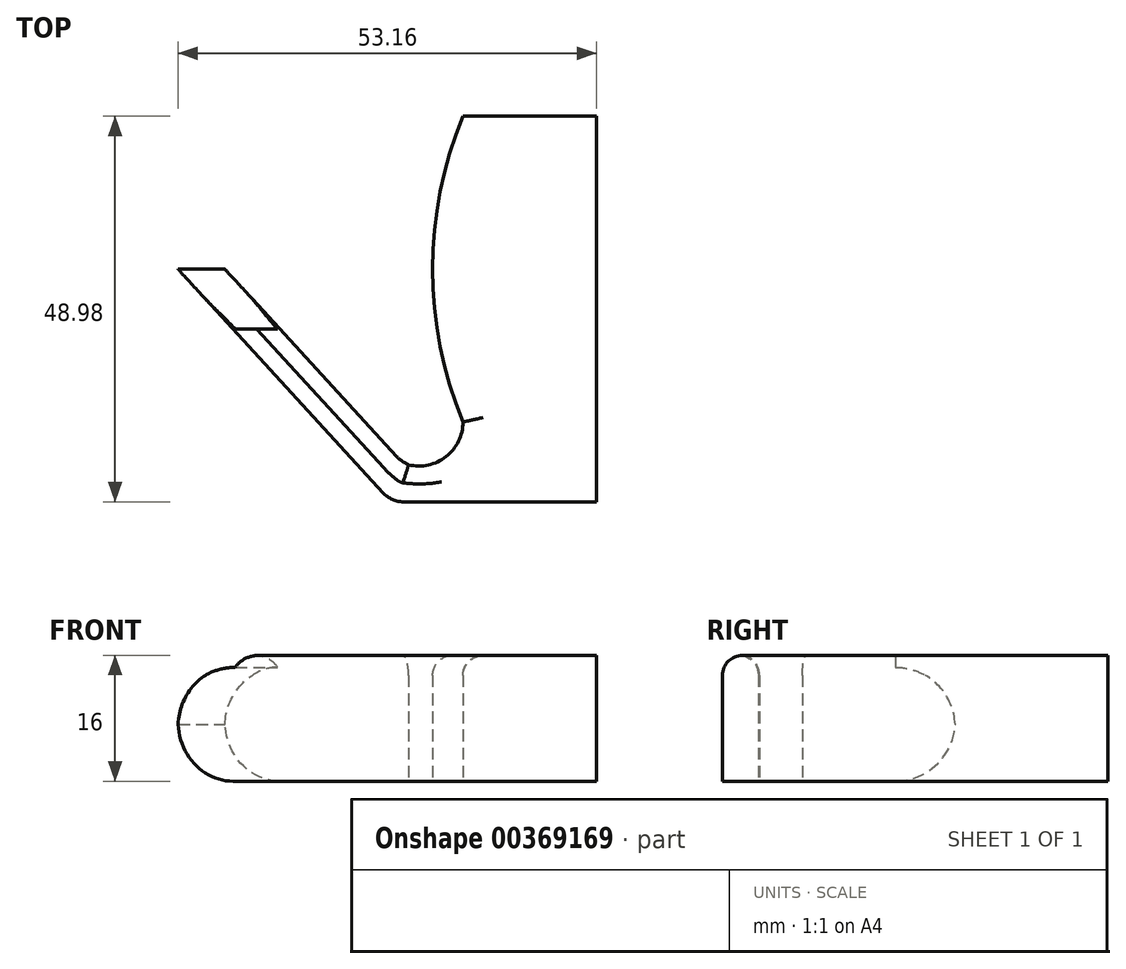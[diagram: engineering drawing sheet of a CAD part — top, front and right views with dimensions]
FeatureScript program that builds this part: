
annotation { "Feature Type Name" : "Feature", "Feature Type Description" : "" }
export const myFeature = defineFeature(function(context is Context, id is Id, definition is map)
    precondition{}
    {
        {
            var Q0;
            Q0=qCreatedBy(makeId("Top.planeOp"),FACE);
            var sketch = newSketch(context, id + "F0", { "sketchPlane" : qUnion([Q0])});
            skLineSegment(sketch, "E0.bottom", {"start": v(16.97, 19.42) * mm, "end": v(-16.97, 19.42) * mm});
            skLineSegment(sketch, "E0.top", {"start": v(16.97, -19.42) * mm, "end": v(-16.97, -19.42) * mm});
            skLineSegment(sketch, "E0.left", {"start": v(16.97, 19.42) * mm, "end": v(16.97, -19.42) * mm});
            skLineSegment(sketch, "E0.right", {"start": v(-16.97, 19.42) * mm, "end": v(-16.97, -19.42) * mm});
            skPoint(sketch, "E0.middle", {"position": v(0, 0) * mm});
            skArc(sketch, "E1", {"start": v(-16.97, 19.42) * mm, "mid": v(-20.82, 0) * mm, "end": v(-16.97, -19.42) * mm});
            skLineSegment(sketch, "E2", {"start": v(0, 19.42) * mm, "end": v(0, -19.42) * mm});
            skLineSegment(sketch, "E3", {"start": v(0, -19.42) * mm, "end": v(0, -29.56) * mm});
            skLineSegment(sketch, "E4", {"start": v(0, -29.56) * mm, "end": v(-24.5, -29.56) * mm});
            skArc(sketch, "E5", {"start": v(-27.11, -28.41) * mm, "mid": v(-25.93, -29.26) * mm, "end": v(-24.5, -29.56) * mm});
            skLineSegment(sketch, "E6", {"start": v(-27.11, -28.41) * mm, "end": v(-53.17, 0) * mm});
            skLineSegment(sketch, "E7", {"start": v(-53.17, 0) * mm, "end": v(-47.22, 0) * mm});
            skLineSegment(sketch, "E8", {"start": v(-47.22, 0) * mm, "end": v(-25.4, -23.79) * mm});
            skArc(sketch, "E9", {"start": v(-25.4, -23.79) * mm, "mid": v(-24.7, -24.4) * mm, "end": v(-23.87, -24.86) * mm});
            skArc(sketch, "E10", {"start": v(-23.87, -24.86) * mm, "mid": v(-19.1, -23.8) * mm, "end": v(-16.97, -19.42) * mm});
            skLineSegment(sketch, "E11", {"start": v(-45.18, -8.7) * mm, "end": v(-39.23, -8.7) * mm});
            skSolve(sketch);
        }
        {
            var Q0;
            {var subQ1=sQuery(id+"F0.wireOp",EDGE,"E3");Q0=makeQuery(id+"F0.imprint","IMPRINT",FACE,{"disambiguationData":[TD([[makeQuery(id+"F0.imprint","IMPRINT",EDGE,{"derivedFrom":subQ1}),-1.0]])]});}
            var Q1;
            {var subQ1=sQuery(id+"F0.wireOp",EDGE,"E0.right");Q1=makeQuery(id+"F0.imprint","IMPRINT",FACE,{"disambiguationData":[TD([[makeQuery(id+"F0.imprint","IMPRINT",EDGE,{"derivedFrom":subQ1}),1.0]])]});}
            var Q2;
            Q2=makeQuery(id+"F0.imprint","IMPRINT",FACE,{"disambiguationData":[TD([[makeQuery(id+"F0.imprint","IMPRINT",EDGE,{"derivedFrom":sQuery(id+"F0.wireOp",EDGE,"E0.right")}),-1.0]])]});
            var Q3;
            {var subQ0=sQuery(id+"F0.wireOp",EDGE,"E7");Q3=makeQuery(id+"F0.imprint","IMPRINT",FACE,{"disambiguationData":[TD([[makeQuery(id+"F0.imprint","IMPRINT",EDGE,{"derivedFrom":subQ0}),-1.0]])]});}
            extrude(context, id + "F1", {"entities" : qUnion([Q0, Q1, Q2, Q3]), "depth" : 14.48 * mm});
        }
        {
            var Q0;
            Q0=makeQuery(id+"F1.opExtrude","CAP_EDGE",EDGE,{"disambiguationData":[OSD([sQuery(id+"F0.wireOp",EDGE,"E7")])],"isStart":false});
            var Q1;
            Q1=makeQuery(id+"F1.opExtrude","CAP_EDGE",EDGE,{"disambiguationData":[OSD([sQuery(id+"F0.wireOp",EDGE,"E7")])],"isStart":true});
            fillet(context, id + "F2", {"entities" : qUnion([Q0, Q1]), "radius" : 7.62 * mm, "tangentPropagation" : true, "allowEdgeOverflow" : false});
        }
        {
            var Q0;
            Q0=makeQuery(id+"F1.opExtrude","CAP_FACE",FACE,{"disambiguationData":[OSD([sQuery(id+"F0.wireOp",EDGE,"E0.bottom"),sQuery(id+"F0.wireOp",EDGE,"E1"),sQuery(id+"F0.wireOp",EDGE,"E2"),sQuery(id+"F0.wireOp",EDGE,"E3"),sQuery(id+"F0.wireOp",EDGE,"E4"),sQuery(id+"F0.wireOp",EDGE,"E5"),sQuery(id+"F0.wireOp",EDGE,"E6"),sQuery(id+"F0.wireOp",EDGE,"E7"),sQuery(id+"F0.wireOp",EDGE,"E8"),sQuery(id+"F0.wireOp",EDGE,"E9"),sQuery(id+"F0.wireOp",EDGE,"E10")])],"isStart":false});
            extrude(context, id + "F3", {"entities" : qUnion([Q0]), "operationType" : NewBodyOperationType.ADD, "depth" : 1.52 * mm});
        }
        {
            var Q0;
            Q0=makeQuery(id+"F3.opExtrude","CAP_EDGE",EDGE,{"disambiguationData":[OSD([sQuery(id+"F0.wireOp",EDGE,"E4")])],"isStart":false});
            var Q1;
            Q1=makeQuery(id+"F3.opExtrude","CAP_EDGE",EDGE,{"disambiguationData":[OSD([sQuery(id+"F0.wireOp",EDGE,"E5")])],"isStart":false});
            var Q2;
            Q2=makeQuery(id+"F3.opExtrude","CAP_EDGE",EDGE,{"disambiguationData":[OSD([sQuery(id+"F0.wireOp",EDGE,"E6")])],"isStart":false});
            var Q3;
            Q3=makeQuery(id+"F3.opExtrude","CAP_EDGE",EDGE,{"disambiguationData":[OSD([sQuery(id+"F0.wireOp",EDGE,"E8")])],"isStart":false});
            var Q4;
            Q4=makeQuery(id+"F3.opExtrude","CAP_EDGE",EDGE,{"disambiguationData":[OSD([sQuery(id+"F0.wireOp",EDGE,"E10")])],"isStart":false});
            var Q5;
            Q5=makeQuery(id+"F3.opExtrude","CAP_EDGE",EDGE,{"disambiguationData":[OSD([sQuery(id+"F0.wireOp",EDGE,"E1")])],"isStart":false});
            fillet(context, id + "F4", {"entities" : qUnion([Q0, Q1, Q2, Q3, Q4, Q5]), "radius" : 2.54 * mm, "tangentPropagation" : true, "allowEdgeOverflow" : false});
        }
    });
